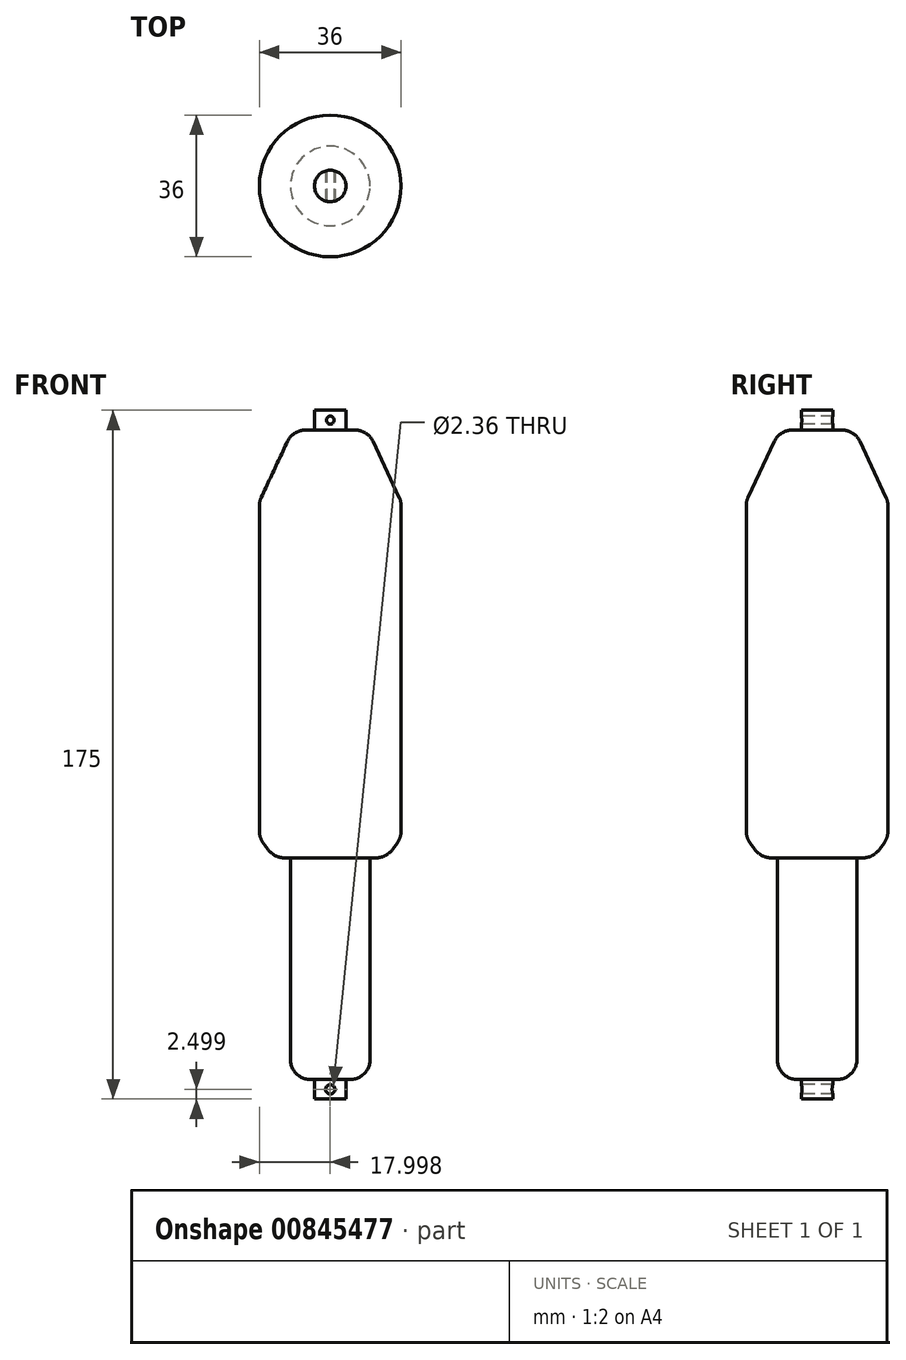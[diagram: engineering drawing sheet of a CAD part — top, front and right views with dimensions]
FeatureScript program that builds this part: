
annotation { "Feature Type Name" : "Feature", "Feature Type Description" : "" }
export const myFeature = defineFeature(function(context is Context, id is Id, definition is map)
    precondition{}
    {
        {
            var Q0;
            Q0=qCreatedBy(makeId("Front.planeOp"),FACE);
            var sketch = newSketch(context, id + "F0", { "sketchPlane" : qUnion([Q0])});
            skLineSegment(sketch, "E0", {"start": v(-5.8, 86.35) * mm, "end": v(-12.12, 86.35) * mm});
            skLineSegment(sketch, "E1", {"start": v(-16.64, 83.47) * mm, "end": v(-23.32, 69.24) * mm});
            skLineSegment(sketch, "E2", {"start": v(-23.8, 67.12) * mm, "end": v(-23.8, -15.6) * mm});
            skLineSegment(sketch, "E3", {"start": v(-22.84, -18.55) * mm, "end": v(-21.57, -20.28) * mm});
            skLineSegment(sketch, "E4", {"start": v(-17.53, -22.34) * mm, "end": v(-15.9, -22.34) * mm});
            skLineSegment(sketch, "E5", {"start": v(-15.9, -22.34) * mm, "end": v(-15.9, -73.65) * mm});
            skLineSegment(sketch, "E6", {"start": v(-10.9, -78.65) * mm, "end": v(-9.8, -78.65) * mm});
            skLineSegment(sketch, "E7", {"start": v(-9.8, -78.65) * mm, "end": v(-9.8, -83.65) * mm});
            skLineSegment(sketch, "E8", {"start": v(-9.8, -83.65) * mm, "end": v(-5.8, -83.65) * mm});
            skLineSegment(sketch, "E9", {"start": v(-5.8, -83.65) * mm, "end": v(-5.8, 86.35) * mm});
            skPoint(sketch, "E10.visualSharp", {"position": v(-15.3, 86.35) * mm});
            skArc(sketch, "E10.filletArc", {"start": v(-12.12, 86.35) * mm, "mid": v(-14.8, 85.57) * mm, "end": v(-16.64, 83.47) * mm});
            skPoint(sketch, "E11.visualSharp", {"position": v(-23.8, 68.23) * mm});
            skArc(sketch, "E11.filletArc", {"start": v(-23.32, 69.24) * mm, "mid": v(-23.67, 68.2) * mm, "end": v(-23.8, 67.12) * mm});
            skPoint(sketch, "E12.visualSharp", {"position": v(-23.8, -17.23) * mm});
            skArc(sketch, "E12.filletArc", {"start": v(-23.8, -15.6) * mm, "mid": v(-23.55, -17.15) * mm, "end": v(-22.84, -18.55) * mm});
            skPoint(sketch, "E13.visualSharp", {"position": v(-20.08, -22.34) * mm});
            skArc(sketch, "E13.filletArc", {"start": v(-21.57, -20.28) * mm, "mid": v(-19.8, -21.8) * mm, "end": v(-17.53, -22.34) * mm});
            skPoint(sketch, "E14.visualSharp", {"position": v(-15.9, -78.65) * mm});
            skArc(sketch, "E14.filletArc", {"start": v(-15.9, -73.65) * mm, "mid": v(-14.43, -77.2) * mm, "end": v(-10.9, -78.65) * mm});
            skLineSegment(sketch, "E15", {"start": v(-5.8, 86.35) * mm, "end": v(-5.8, 91.35) * mm});
            skLineSegment(sketch, "E16", {"start": v(-5.8, 91.35) * mm, "end": v(-9.8, 91.35) * mm});
            skLineSegment(sketch, "E17", {"start": v(-9.8, 91.35) * mm, "end": v(-9.8, 86.35) * mm});
            skLineSegment(sketch, "E18", {"start": v(-9.8, 86.35) * mm, "end": v(-5.8, 86.35) * mm});
            skPoint(sketch, "E19.centerSnap0", {"position": v(-9.8, -81.15) * mm});
            skPoint(sketch, "E19.centerSnap1", {"position": v(-7.8, -83.65) * mm});
            skLineSegment(sketch, "E20", {"start": v(-9.8, -81.15) * mm, "end": v(-2.03, -81.15) * mm, "construction": true});
            skSolve(sketch);
        }
        {
            var Q0;
            Q0=makeQuery(id+"F0.imprint","IMPRINT",FACE,{"disambiguationData":[TD([[makeQuery(id+"F0.imprint","IMPRINT",EDGE,{"derivedFrom":sQuery(id+"F0.wireOp",EDGE,"E0")}),1.0]])]});
            var Q1;
            Q1=makeQuery(id+"F0.imprint","IMPRINT",FACE,{"disambiguationData":[TD([[makeQuery(id+"F0.imprint","IMPRINT",EDGE,{"derivedFrom":sQuery(id+"F0.wireOp",EDGE,"E15")}),1.0]])]});
            var Q2;
            Q2=sQuery(id+"F0.wireOp",EDGE,"E9");
            revolve(context, id + "F1", {"surfaceOperationType" : NewSurfaceOperationType.NEW, "entities" : qUnion([Q0, Q1]), "axis" : qUnion([Q2]), "revolveType" : RevolveType.FULL});
        }
        {
            var Q0;
            Q0=qCreatedBy(makeId("Front.planeOp"),FACE);
            var sketch = newSketch(context, id + "F2", { "sketchPlane" : qUnion([Q0])});
            skCircle(sketch, "E21", {"center": v(-5.8, 88.85) * mm, "radius": 1 * mm});
            skCircle(sketch, "E22", {"center": v(-5.8, -81.15) * mm, "radius": 1.18 * mm});
            skSolve(sketch);
        }
        {
            var Q0;
            Q0=makeQuery(id+"F2.imprint","IMPRINT",FACE,{"disambiguationData":[TD([[makeQuery(id+"F2.imprint","IMPRINT",EDGE,{"derivedFrom":sQuery(id+"F2.wireOp",EDGE,"E21")}),1.0]])]});
            var Q1;
            Q1=makeQuery(id+"F2.imprint","IMPRINT",FACE,{"disambiguationData":[TD([[makeQuery(id+"F2.imprint","IMPRINT",EDGE,{"derivedFrom":sQuery(id+"F2.wireOp",EDGE,"E22")}),1.0]])]});
            extrude(context, id + "F3", {"entities" : qUnion([Q0, Q1]), "operationType" : NewBodyOperationType.REMOVE, "endBound" : BoundingType.SYMMETRIC, "oppositeDirection" : true, "depth" : 8 * mm, "offsetDistance" : 25 * mm});
        }
    });
